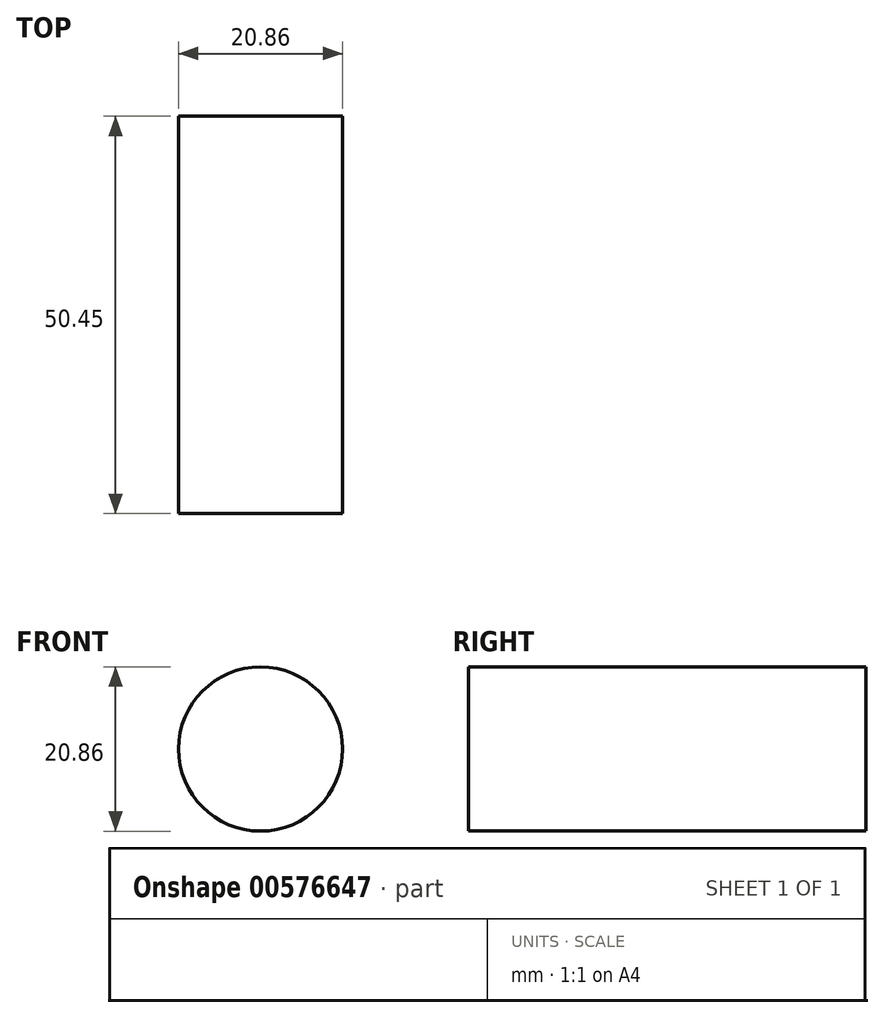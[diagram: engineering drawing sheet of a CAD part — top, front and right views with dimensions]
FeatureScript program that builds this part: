
annotation { "Feature Type Name" : "Feature", "Feature Type Description" : "" }
export const myFeature = defineFeature(function(context is Context, id is Id, definition is map)
    precondition{}
    {
        {
            var Q0;
            Q0=qCreatedBy(makeId("Front.planeOp"),FACE);
            var sketch = newSketch(context, id + "F0", { "sketchPlane" : qUnion([Q0])});
            skCircle(sketch, "E0", {"center": v(0, 0) * mm, "radius": 10.43 * mm});
            skSolve(sketch);
        }
        {
            var Q0;
            Q0 = qSketchRegion(id + "F0", true);
            extrude(context, id + "F1", {"entities" : qUnion([Q0]), "depth" : 50.45 * mm, "offsetDistance" : 25.4 * mm});
        }
    });
